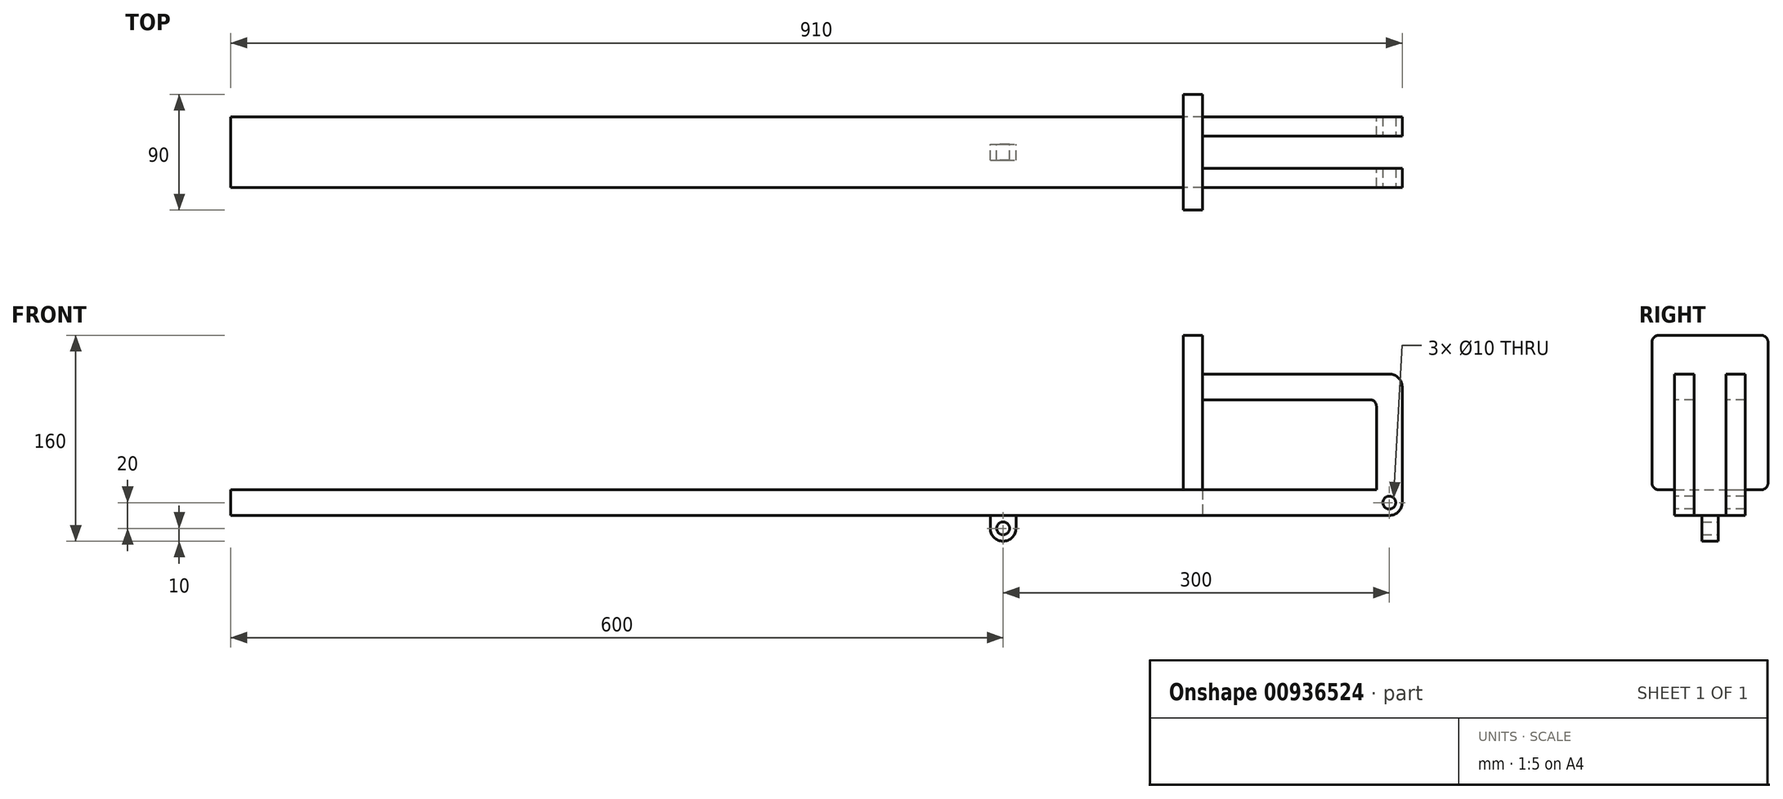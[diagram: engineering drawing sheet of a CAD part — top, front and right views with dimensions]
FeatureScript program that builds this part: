
annotation { "Feature Type Name" : "Feature", "Feature Type Description" : "" }
export const myFeature = defineFeature(function(context is Context, id is Id, definition is map)
    precondition{}
    {
        {
            var Q0;
            Q0=qCreatedBy(makeId("Front.planeOp"),FACE);
            var sketch = newSketch(context, id + "F0", { "sketchPlane" : qUnion([Q0])});
            skCircle(sketch, "E0", {"center": v(0, 0) * mm, "radius": 5 * mm});
            skArc(sketch, "E1", {"start": v(0, -10) * mm, "mid": v(10, 0) * mm, "end": v(0, 10) * mm});
            skLineSegment(sketch, "E2", {"start": v(0, 10) * mm, "end": v(-900, 10) * mm});
            skLineSegment(sketch, "E3", {"start": v(0, -10) * mm, "end": v(-900, -10) * mm});
            skLineSegment(sketch, "E4", {"start": v(-900, -10) * mm, "end": v(-900, 10) * mm});
            skSolve(sketch);
        }
        {
            var Q0;
            Q0=makeQuery(id+"F0.imprint","IMPRINT",FACE,{"disambiguationData":[TD([[makeQuery(id+"F0.imprint","IMPRINT",EDGE,{"derivedFrom":sQuery(id+"F0.wireOp",EDGE,"E0")}),-1.0]])]});
            extrude(context, id + "F1", {"entities" : qUnion([Q0]), "oppositeDirection" : true, "depth" : 27.5 * mm, "offsetDistance" : 25 * mm, "hasSecondDirection" : true, "secondDirectionOppositeDirection" : false, "secondDirectionDepth" : 27.5 * mm});
        }
        {
            var Q0;
            Q0=makeQuery(id+"F1.opExtrude","CAP_FACE",FACE,{"disambiguationData":[OSD([sQuery(id+"F0.wireOp",EDGE,"E0"),sQuery(id+"F0.wireOp",EDGE,"E1"),sQuery(id+"F0.wireOp",EDGE,"E2"),sQuery(id+"F0.wireOp",EDGE,"E3"),sQuery(id+"F0.wireOp",EDGE,"E4")])],"isStart":true});
            cPlane(context, id + "F2", {"entities" : qUnion([Q0]), "cplaneType" : CPlaneType.OFFSET, "offset" : 27.5 * mm, "oppositeDirection" : true, "width" : 150 * mm, "height" : 150 * mm});
        }
        {
            var Q0;
            Q0=makeQuery(id+"F1.opExtrude","CAP_FACE",FACE,{"disambiguationData":[OSD([sQuery(id+"F0.wireOp",EDGE,"E0"),sQuery(id+"F0.wireOp",EDGE,"E1"),sQuery(id+"F0.wireOp",EDGE,"E2"),sQuery(id+"F0.wireOp",EDGE,"E3"),sQuery(id+"F0.wireOp",EDGE,"E4")])],"isStart":true});
            cPlane(context, id + "F3", {"entities" : qUnion([Q0]), "cplaneType" : CPlaneType.OFFSET, "offset" : 0 * mm, "width" : 150 * mm, "height" : 150 * mm});
        }
        {
            var Q0;
            Q0=qCreatedBy(id+"F3.planeOp",FACE);
            var sketch = newSketch(context, id + "F4", { "sketchPlane" : qUnion([Q0])});
            skArc(sketch, "E5", {"start": v(-10, 0) * mm, "mid": v(0, -10) * mm, "end": v(10, 0) * mm});
            skLineSegment(sketch, "E6", {"start": v(10, 0) * mm, "end": v(10, 90) * mm});
            skArc(sketch, "E7", {"start": v(10, 90) * mm, "mid": v(7.07, 97.07) * mm, "end": v(0, 100) * mm});
            skLineSegment(sketch, "E8", {"start": v(0, 100) * mm, "end": v(-145, 100) * mm});
            skLineSegment(sketch, "E9", {"start": v(-145, 100) * mm, "end": v(-145, 80) * mm});
            skLineSegment(sketch, "E10", {"start": v(-145, 80) * mm, "end": v(-10, 80) * mm});
            skLineSegment(sketch, "E11", {"start": v(-10, 0) * mm, "end": v(-10, 80) * mm});
            skLineSegment(sketch, "E12", {"start": v(-145, 80) * mm, "end": v(-145, 10) * mm});
            skPoint(sketch, "E13.orphan", {"position": v(0, 80) * mm});
            skCircle(sketch, "E14", {"center": v(0, 0) * mm, "radius": 5 * mm});
            skSolve(sketch);
        }
        {
            var Q0;
            Q0=makeQuery(id+"F4.imprint","IMPRINT",FACE,{"disambiguationData":[TD([[makeQuery(id+"F4.imprint","IMPRINT",EDGE,{"derivedFrom":sQuery(id+"F4.wireOp",EDGE,"E5")}),1.0]])]});
            extrude(context, id + "F5", {"entities" : qUnion([Q0]), "operationType" : NewBodyOperationType.ADD, "oppositeDirection" : true, "depth" : 55 * mm, "offsetDistance" : 25 * mm});
        }
        {
            var Q0;
            Q0=qCreatedBy(id+"F2.planeOp",FACE);
            var sketch = newSketch(context, id + "F6", { "sketchPlane" : qUnion([Q0])});
            skLineSegment(sketch, "E15", {"start": v(30, -18.24) * mm, "end": v(30, 107.92) * mm});
            skLineSegment(sketch, "E16", {"start": v(30, 107.92) * mm, "end": v(-145, 107.92) * mm});
            skLineSegment(sketch, "E17", {"start": v(-145, 107.92) * mm, "end": v(-145, -18.24) * mm});
            skLineSegment(sketch, "E18", {"start": v(30, -18.24) * mm, "end": v(-145, -18.24) * mm});
            skSolve(sketch);
        }
        {
            var Q0;
            Q0=makeQuery(id+"F6.imprint","IMPRINT",FACE,{"disambiguationData":[TD([[makeQuery(id+"F6.imprint","IMPRINT",EDGE,{"derivedFrom":sQuery(id+"F6.wireOp",EDGE,"E15")}),1.0]])]});
            extrude(context, id + "F7", {"entities" : qUnion([Q0]), "operationType" : NewBodyOperationType.REMOVE, "oppositeDirection" : true, "depth" : 12.5 * mm, "offsetDistance" : 25 * mm, "hasSecondDirection" : true, "secondDirectionOppositeDirection" : false, "secondDirectionDepth" : 12.5 * mm});
        }
        {
            var Q0;
            Q0=qCreatedBy(id+"F2.planeOp",FACE);
            var sketch = newSketch(context, id + "F8", { "sketchPlane" : qUnion([Q0])});
            skLineSegment(sketch, "E19", {"start": v(0, 0) * mm, "end": v(-300, 0) * mm});
            skLineSegment(sketch, "E20", {"start": v(-300, 0) * mm, "end": v(-300, -10) * mm});
            skArc(sketch, "E21", {"start": v(-310, -20) * mm, "mid": v(-300, -30) * mm, "end": v(-290, -20) * mm});
            skCircle(sketch, "E22", {"center": v(-300, -20) * mm, "radius": 5 * mm});
            skLineSegment(sketch, "E23", {"start": v(-295, -20) * mm, "end": v(-290, -20) * mm});
            skLineSegment(sketch, "E24", {"start": v(-290, -20) * mm, "end": v(-290, -10) * mm});
            skLineSegment(sketch, "E25", {"start": v(-310, -20) * mm, "end": v(-310, -10) * mm});
            skLineSegment(sketch, "E26", {"start": v(-310, -10) * mm, "end": v(-290, -10) * mm});
            skPoint(sketch, "E27.orphan", {"position": v(-300, -30) * mm});
            skSolve(sketch);
        }
        {
            var Q0;
            Q0=makeQuery(id+"F8.imprint","IMPRINT",FACE,{"disambiguationData":[TD([[makeQuery(id+"F8.imprint","IMPRINT",EDGE,{"derivedFrom":sQuery(id+"F8.wireOp",EDGE,"E21")}),1.0]])]});
            extrude(context, id + "F9", {"entities" : qUnion([Q0]), "operationType" : NewBodyOperationType.ADD, "depth" : 6.25 * mm, "offsetDistance" : 25 * mm, "hasSecondDirection" : true, "secondDirectionOppositeDirection" : true, "secondDirectionDepth" : 6.25 * mm});
        }
        {
            var Q0;
            Q0=qCreatedBy(id+"F2.planeOp",FACE);
            var sketch = newSketch(context, id + "F10", { "sketchPlane" : qUnion([Q0])});
            skLineSegment(sketch, "E28", {"start": v(0, 0) * mm, "end": v(0, 10) * mm});
            skLineSegment(sketch, "E29", {"start": v(0, 10) * mm, "end": v(-145, 10) * mm});
            skLineSegment(sketch, "E30", {"start": v(-145, 10) * mm, "end": v(-145, 130) * mm});
            skLineSegment(sketch, "E31", {"start": v(-145, 130) * mm, "end": v(-160, 130) * mm});
            skLineSegment(sketch, "E32", {"start": v(-160, 130) * mm, "end": v(-160, 10) * mm});
            skLineSegment(sketch, "E33", {"start": v(-160, 10) * mm, "end": v(-145, 10) * mm});
            skSolve(sketch);
        }
        {
            var Q0;
            Q0=makeQuery(id+"F10.imprint","IMPRINT",FACE,{"disambiguationData":[TD([[makeQuery(id+"F10.imprint","IMPRINT",EDGE,{"derivedFrom":sQuery(id+"F10.wireOp",EDGE,"E30")}),1.0]])]});
            extrude(context, id + "F11", {"entities" : qUnion([Q0]), "operationType" : NewBodyOperationType.ADD, "depth" : 45 * mm, "offsetDistance" : 25 * mm, "hasSecondDirection" : true, "secondDirectionOppositeDirection" : true, "secondDirectionDepth" : 45 * mm});
        }
        {
            var Q0;
            Q0=makeQuery(id+"F11.opExtrude","CAP_EDGE",EDGE,{"disambiguationData":[OSD([sQuery(id+"F10.wireOp",EDGE,"E31")])],"isStart":false});
            var Q1;
            Q1=makeQuery(id+"F11.opExtrude","CAP_EDGE",EDGE,{"disambiguationData":[OSD([sQuery(id+"F10.wireOp",EDGE,"E31")])],"isStart":true});
            var Q2;
            Q2=makeQuery(id+"F11.opExtrude","CAP_EDGE",EDGE,{"disambiguationData":[OSD([sQuery(id+"F10.wireOp",EDGE,"E33")])],"isStart":false});
            var Q3;
            Q3=makeQuery(id+"F11.opExtrude","CAP_EDGE",EDGE,{"disambiguationData":[OSD([sQuery(id+"F10.wireOp",EDGE,"E33")])],"isStart":true});
            fillet(context, id + "F12", {"entities" : qUnion([Q0, Q1, Q2, Q3]), "radius" : 5 * mm, "tangentPropagation" : true, "allowEdgeOverflow" : false});
        }
        {
            var Q0;
            {var subQ0=sQuery(id+"F4.wireOp",EDGE,"E11");var subQ1=sQuery(id+"F4.wireOp",EDGE,"E10");Q0=makeQuery(id+"F7.boolean.opBoolean","SPLIT",EDGE,{"disambiguationData":[TD([makeQuery(id+"F7.opExtrude","CAP_FACE",FACE,{"disambiguationData":[OSD([sQuery(id+"F6.wireOp",EDGE,"E15"),sQuery(id+"F6.wireOp",EDGE,"E16"),sQuery(id+"F6.wireOp",EDGE,"E17"),sQuery(id+"F6.wireOp",EDGE,"E18")])],"isStart":true})])],"derivedFrom":makeQuery(id+"F5.opExtrude","SWEPT_EDGE",EDGE,{"disambiguationData":[OSD([subQ1,subQ0])]})});}
            var Q1;
            {var subQ0=sQuery(id+"F4.wireOp",EDGE,"E11");var subQ1=sQuery(id+"F4.wireOp",EDGE,"E10");Q1=makeQuery(id+"F7.boolean.opBoolean","SPLIT",EDGE,{"disambiguationData":[TD([makeQuery(id+"F7.opExtrude","CAP_FACE",FACE,{"disambiguationData":[OSD([sQuery(id+"F6.wireOp",EDGE,"E15"),sQuery(id+"F6.wireOp",EDGE,"E16"),sQuery(id+"F6.wireOp",EDGE,"E17"),sQuery(id+"F6.wireOp",EDGE,"E18")])],"isStart":false})])],"derivedFrom":makeQuery(id+"F5.opExtrude","SWEPT_EDGE",EDGE,{"disambiguationData":[OSD([subQ1,subQ0])]})});}
            fillet(context, id + "F13", {"entities" : qUnion([Q0, Q1]), "radius" : 5 * mm, "tangentPropagation" : true, "allowEdgeOverflow" : false});
        }
    });
